# Revit family: LF-T16-S-RxX055-15xx
name_source: partatom
category: Leuchten
units: mm (PartAtom-declared; Revit-internal decimal feet)

## family parameters
Basisbauteil = Fläche
Beim Laden mit Abzugskörper schneiden = Nein
Bemaßung runder Anschluss = Durchmesser verwenden
Gemeinsam genutzt = Nein
Lichtquelle = Ja
OmniClass-Nummer = 23.80.70.11
OmniClass-Titel = Luminaries for Internal Lighting
Raumberechnungspunkt = Nein
Teiletyp = Normal

## types (8) — shared parameters
Baugruppenkennzeichen = D5020200
Emissionsform beim Rendern sichtbar = Nein
Farbfilter = 16777215
Farbtemperaturverschiebung bei Dämpfen der Lampe = <Keine Auswahl>
Hersteller = RIDI Leuchten GmbH
Lampe = LED
Neigungswinkel = 90.00°
URL = www.ridi.de
Von Breite des Rechtecks ausssenden = 592 mm  [stored 1.94226 ft]
Von Länge des Rechtecks aussenden = 85 mm  [stored 0.278871 ft]
brand = RIDI
conformity mark = CE
electrical safety class = 1
height = 72 mm  [stored 0.23622 ft]
ingress protection (IP) code = IP64
length = 598 mm  [stored 1.96194 ft]
nominal frequency = 50-60Hz
nominal voltage = 230
voltage type (AC, DC, UC) = AC
width = 85 mm  [stored 0.278871 ft]
zero-valued in all types: Vorgabe-Ansicht

## per-type parameters (varying)
| type | Datei für fotometrisches Netz | Modell | Scheinlast | rated input power | weight |
| LF-T16-S-R1X055/15ND-SM | LF-T16-S-R1xxx-SM.IES | 0450010 | 9 VA | 9 | 1,18 kg |
| LF-T16-S-R1X055/15DA-SM | LF-T16-S-R1xxx-SM.IES | 0460010 | 9 VA | 9 | 1,18 kg |
| LF-T16-S-R1X055/15ND-OE | LF-T16-S-R1xxx-OE.IES | 0450012 | 15 VA | 15 | 1,09 kg |
| LF-T16-S-R1X055/15DA-OE | LF-T16-S-R1xxx-OE.IES | 0460012 | 15 VA | 15 | 1,09 kg |
| LF-T16-S-R2X055/15ND-OE | LF-T16-S-R2xxx-OE.IES | 0450062 | 30 VA | 30 | 1,53 kg |
| LF-T16-S-R2X055/15DA-OE | LF-T16-S-R2xxx-OE.IES | 0460062 | 30 VA | 30 | 1,53 kg |
| LF-T16-S-R1X055/15ND-AS | LF-T16-S-R1xxx-AS.IES | 0450014 | 9 VA | 9 | 1,29 kg |
| LF-T16-S-R1X055/15DA-AS | LF-T16-S-R1xxx-AS.IES | 0460014 | 9 VA | 9 | 1,29 kg |

note: column(s) folded — value = type name in every type: product name

note: [stored X ft] marks values corroborated as IEEE doubles in the binary element streams (Revit-internal decimal feet)
